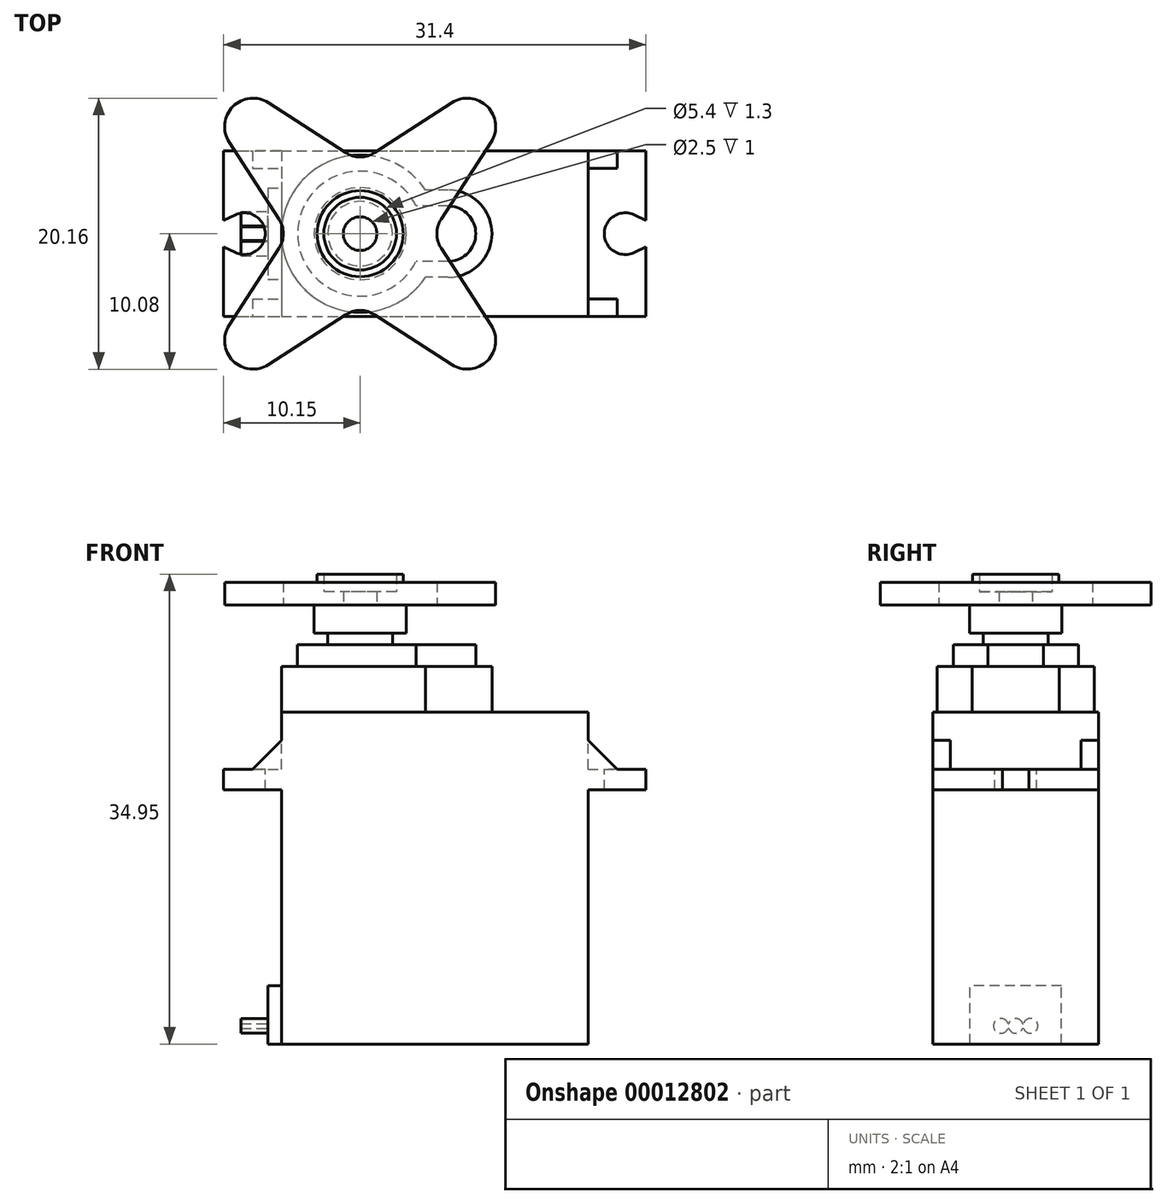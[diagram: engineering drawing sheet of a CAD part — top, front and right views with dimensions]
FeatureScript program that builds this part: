
annotation { "Feature Type Name" : "Feature", "Feature Type Description" : "" }
export const myFeature = defineFeature(function(context is Context, id is Id, definition is map)
    precondition{}
    {
        {
            var Q0;
            Q0=qCreatedBy(makeId("Top.planeOp"),FACE);
            var sketch = newSketch(context, id + "F0", { "sketchPlane" : qUnion([Q0])});
            skArc(sketch, "E0", {"start": v(4.86, 3.25) * mm, "mid": v(-5.85, 0) * mm, "end": v(4.86, -3.25) * mm});
            skLineSegment(sketch, "E1.bottom", {"start": v(-10.15, 6.15) * mm, "end": v(21.25, 6.15) * mm});
            skLineSegment(sketch, "E1.top", {"start": v(-10.15, -6.15) * mm, "end": v(21.25, -6.15) * mm});
            skLineSegment(sketch, "E1.left", {"start": v(-10.15, 6.15) * mm, "end": v(-10.15, 0) * mm});
            skLineSegment(sketch, "E1.right", {"start": v(21.25, 6.15) * mm, "end": v(21.25, 0) * mm});
            skLineSegment(sketch, "E2", {"start": v(-5.85, 6.15) * mm, "end": v(-5.85, -6.15) * mm});
            skLineSegment(sketch, "E3", {"start": v(16.95, 6.15) * mm, "end": v(16.95, -6.15) * mm});
            skCircle(sketch, "E4", {"center": v(-8.6, 0) * mm, "radius": 1.55 * mm});
            skPoint(sketch, "E5", {"position": v(21.25, 0) * mm});
            skLineSegment(sketch, "E6", {"start": v(5.55, 6.15) * mm, "end": v(5.55, -6.15) * mm, "construction": true});
            skArc(sketch, "E7", {"start": v(6.55, -3.25) * mm, "mid": v(9.8, 0) * mm, "end": v(6.55, 3.25) * mm});
            skLineSegment(sketch, "E8", {"start": v(6.55, -3.25) * mm, "end": v(4.86, -3.25) * mm});
            skLineSegment(sketch, "E9", {"start": v(6.55, 3.25) * mm, "end": v(4.86, 3.25) * mm});
            skArc(sketch, "E10.0", {"start": v(4.17, 2.05) * mm, "mid": v(-4.65, 0) * mm, "end": v(4.17, -2.05) * mm});
            skLineSegment(sketch, "E10.1", {"start": v(6.55, 2.05) * mm, "end": v(4.17, 2.05) * mm});
            skArc(sketch, "E10.2", {"start": v(6.55, -2.05) * mm, "mid": v(8.6, 0) * mm, "end": v(6.55, 2.05) * mm});
            skLineSegment(sketch, "E10.3", {"start": v(6.55, -2.05) * mm, "end": v(4.17, -2.05) * mm});
            skCircle(sketch, "E11", {"center": v(0, 0) * mm, "radius": 2.4 * mm});
            skLineSegment(sketch, "E12", {"start": v(-10.15, 0) * mm, "end": v(-10.15, -6.15) * mm});
            skLineSegment(sketch, "E13", {"start": v(21.25, 0) * mm, "end": v(21.25, -6.15) * mm});
            skLineSegment(sketch, "E14", {"start": v(-9.28, 1.4) * mm, "end": v(-12.15, 0) * mm});
            skLineSegment(sketch, "E15", {"start": v(-12.15, 0) * mm, "end": v(-9.28, -1.4) * mm});
            skCircle(sketch, "E16.0.MirrorC", {"center": v(19.7, 0) * mm, "radius": 1.55 * mm});
            skLineSegment(sketch, "E17.0.MirrorCS", {"start": v(20.38, 1.4) * mm, "end": v(23.25, 0) * mm});
            skLineSegment(sketch, "E18.0.MirrorCS", {"start": v(23.25, 0) * mm, "end": v(20.38, -1.4) * mm});
            skSolve(sketch);
        }
        {
            var Q0;
            {var subQ1=sQuery(id+"F0.wireOp",EDGE,"E3");Q0=makeQuery(id+"F0.imprint","IMPRINT",FACE,{"disambiguationData":[TD([[makeQuery(id+"F0.imprint","IMPRINT",EDGE,{"derivedFrom":subQ1}),-1.0]])]});}
            var Q1;
            Q1=makeQuery(id+"F0.imprint","IMPRINT",FACE,{"disambiguationData":[TD([[makeQuery(id+"F0.imprint","IMPRINT",EDGE,{"derivedFrom":sQuery(id+"F0.wireOp",EDGE,"E7")}),1.0]])]});
            var Q2;
            Q2=makeQuery(id+"F0.imprint","IMPRINT",FACE,{"disambiguationData":[TD([[makeQuery(id+"F0.imprint","IMPRINT",EDGE,{"derivedFrom":sQuery(id+"F0.wireOp",EDGE,"E10.0")}),1.0]])]});
            var Q3;
            Q3=makeQuery(id+"F0.imprint","IMPRINT",FACE,{"disambiguationData":[TD([[makeQuery(id+"F0.imprint","IMPRINT",EDGE,{"derivedFrom":sQuery(id+"F0.wireOp",EDGE,"E11")}),1.0]])]});
            extrude(context, id + "F1", {"entities" : qUnion([Q0, Q1, Q2, Q3]), "oppositeDirection" : true, "depth" : 24.7 * mm});
        }
        {
            var Q0;
            Q0=makeQuery(id+"F0.imprint","IMPRINT",FACE,{"disambiguationData":[TD([[makeQuery(id+"F0.imprint","IMPRINT",EDGE,{"derivedFrom":sQuery(id+"F0.wireOp",EDGE,"E7")}),1.0]])]});
            extrude(context, id + "F2", {"entities" : qUnion([Q0]), "operationType" : NewBodyOperationType.ADD, "depth" : (28.1 - 24.7) * mm});
        }
        {
            var Q0;
            Q0=makeQuery(id+"F0.imprint","IMPRINT",FACE,{"disambiguationData":[TD([[makeQuery(id+"F0.imprint","IMPRINT",EDGE,{"derivedFrom":sQuery(id+"F0.wireOp",EDGE,"E10.0")}),1.0]])]});
            extrude(context, id + "F3", {"entities" : qUnion([Q0]), "operationType" : NewBodyOperationType.ADD, "depth" : (29.7 - 24.7) * mm});
        }
        {
            var Q0;
            Q0=makeQuery(id+"F0.imprint","IMPRINT",FACE,{"disambiguationData":[TD([[makeQuery(id+"F0.imprint","IMPRINT",EDGE,{"derivedFrom":sQuery(id+"F0.wireOp",EDGE,"E11")}),1.0]])]});
            extrude(context, id + "F4", {"entities" : qUnion([Q0]), "operationType" : NewBodyOperationType.ADD, "depth" : (32.65 - 24.7) * mm});
        }
        {
            var Q0;
            {var subQ6=sQuery(id+"F0.wireOp",EDGE,"E1.left");var subQ14=sQuery(id+"F0.wireOp",EDGE,"E1.bottom");var subQ16=makeQuery(id+"F0.imprint","INTERSECT",VERTEX,{"derivedFrom":[subQ14,subQ6]});Q0=makeQuery(id+"F0.imprint","IMPRINT",FACE,{"disambiguationData":[TD([[makeQuery(id+"F0.imprint","IMPRINT",EDGE,{"disambiguationData":[TD([[subQ16,-1.0]])],"derivedFrom":subQ14}),-1.0]])]});}
            var Q1;
            {var subQ11=sQuery(id+"F0.wireOp",EDGE,"E3");Q1=makeQuery(id+"F0.imprint","IMPRINT",FACE,{"disambiguationData":[TD([[makeQuery(id+"F0.imprint","IMPRINT",EDGE,{"derivedFrom":subQ11}),1.0]])]});}
            extrude(context, id + "F5", {"entities" : qUnion([Q0, Q1]), "operationType" : NewBodyOperationType.ADD, "oppositeDirection" : true, "depth" : 5.8 * mm, "hasSecondDirection" : true, "secondDirectionOppositeDirection" : true, "secondDirectionDepth" : (5.8 - 1.55) * mm});
        }
        {
            var Q0;
            {var subQ0=sQuery(id+"F0.wireOp",EDGE,"E2");var subQ1=sQuery(id+"F0.wireOp",EDGE,"E1.top");var subQ3=sQuery(id+"F0.wireOp",EDGE,"E1.bottom");var subQ4=sQuery(id+"F0.wireOp",EDGE,"E3");Q0=makeQuery(id+"F5.boolean.opBoolean","SPLIT",FACE,{"disambiguationData":[TD([makeQuery(id+"F1.opExtrude","CAP_FACE",FACE,{"disambiguationData":[OSD([subQ3,subQ1,subQ0,subQ4])],"isStart":false})])],"derivedFrom":makeQuery(id+"F1.opExtrude","SWEPT_FACE",FACE,{"disambiguationData":[OSD([subQ0])]})});}
            var sketch = newSketch(context, id + "F6", { "sketchPlane" : qUnion([Q0])});
            skLineSegment(sketch, "E19.bottom", {"start": v(-3.4, -24.7) * mm, "end": v(3.4, -24.7) * mm});
            skLineSegment(sketch, "E19.top", {"start": v(-3.4, -20.35) * mm, "end": v(3.4, -20.35) * mm});
            skLineSegment(sketch, "E19.left", {"start": v(-3.4, -24.7) * mm, "end": v(-3.4, -20.35) * mm});
            skLineSegment(sketch, "E19.right", {"start": v(3.4, -24.7) * mm, "end": v(3.4, -20.35) * mm});
            skCircle(sketch, "E20", {"center": v(0, -23.35) * mm, "radius": 0.55 * mm});
            skCircle(sketch, "E21", {"center": v(1.1, -23.35) * mm, "radius": 0.55 * mm});
            skCircle(sketch, "E22", {"center": v(-1.1, -23.35) * mm, "radius": 0.55 * mm});
            skLineSegment(sketch, "E23", {"start": v(0, 0) * mm, "end": v(0, -24.7) * mm, "construction": true});
            skLineSegment(sketch, "E24.rect.bottom", {"start": v(1.1, -23.17) * mm, "end": v(-1.1, -23.17) * mm});
            skLineSegment(sketch, "E24.rect.top", {"start": v(1.1, -23.53) * mm, "end": v(-1.1, -23.53) * mm});
            skLineSegment(sketch, "E24.rect.left", {"start": v(1.1, -23.17) * mm, "end": v(1.1, -23.53) * mm});
            skLineSegment(sketch, "E24.rect.right", {"start": v(-1.1, -23.17) * mm, "end": v(-1.1, -23.53) * mm});
            skSolve(sketch);
        }
        {
            var Q0;
            Q0=makeQuery(id+"F6.imprint","IMPRINT",FACE,{"disambiguationData":[TD([[makeQuery(id+"F6.imprint","IMPRINT",EDGE,{"derivedFrom":sQuery(id+"F6.wireOp",EDGE,"E19.bottom")}),1.0]])]});
            extrude(context, id + "F7", {"entities" : qUnion([Q0]), "operationType" : NewBodyOperationType.ADD, "depth" : 1 * mm});
        }
        {
            var Q0;
            {var subQ0=sQuery(id+"F0.wireOp",EDGE,"E2");var subQ1=sQuery(id+"F0.wireOp",EDGE,"E1.top");var subQ3=sQuery(id+"F0.wireOp",EDGE,"E1.bottom");var subQ4=sQuery(id+"F0.wireOp",EDGE,"E3");var subQ10=sQuery(id+"F6.wireOp",EDGE,"E21");Q0=makeQuery(id+"F7.boolean.opBoolean","SPLIT",FACE,{"disambiguationData":[TD([makeQuery(id+"F7.opExtrude","SWEPT_FACE",FACE,{"disambiguationData":[OSD([subQ10])]})])],"derivedFrom":makeQuery(id+"F5.boolean.opBoolean","SPLIT",FACE,{"disambiguationData":[TD([makeQuery(id+"F1.opExtrude","CAP_FACE",FACE,{"disambiguationData":[OSD([subQ3,subQ1,subQ0,subQ4])],"isStart":false})])],"derivedFrom":makeQuery(id+"F1.opExtrude","SWEPT_FACE",FACE,{"disambiguationData":[OSD([subQ0])]})})});}
            extrude(context, id + "F8", {"entities" : qUnion([Q0]), "operationType" : NewBodyOperationType.ADD, "depth" : 3 * mm});
        }
        {
            var Q0;
            Q0=makeQuery(id+"F4.opExtrude","CAP_FACE",FACE,{"disambiguationData":[OSD([sQuery(id+"F0.wireOp",EDGE,"E11")])],"isStart":false});
            var sketch = newSketch(context, id + "F9", { "sketchPlane" : qUnion([Q0])});
            skCircle(sketch, "E25.0", {"center": v(0, 0) * mm, "radius": 2.4 * mm});
            skCircle(sketch, "E26", {"center": v(0, 0) * mm, "radius": 3.43 * mm});
            skLineSegment(sketch, "E27.rect.bottom", {"start": v(10.07, 10.07) * mm, "end": v(-10.07, 10.08) * mm, "construction": true});
            skLineSegment(sketch, "E27.rect.top", {"start": v(10.07, -10.07) * mm, "end": v(-10.08, -10.07) * mm, "construction": true});
            skLineSegment(sketch, "E27.rect.left", {"start": v(10.07, 10.07) * mm, "end": v(10.07, -10.08) * mm, "construction": true});
            skLineSegment(sketch, "E27.rect.right", {"start": v(-10.07, 10.07) * mm, "end": v(-10.07, -10.07) * mm, "construction": true});
            skLineSegment(sketch, "E28", {"start": v(-10.07, 10.08) * mm, "end": v(10.07, -10.07) * mm, "construction": true});
            skArc(sketch, "E29", {"start": v(-6.82, 9.74) * mm, "mid": v(-9.46, 9.46) * mm, "end": v(-9.74, 6.82) * mm});
            skCircle(sketch, "E30", {"center": v(0, 0) * mm, "radius": 4.47 * mm, "construction": true});
            skLineSegment(sketch, "E31", {"start": v(-6.82, 9.74) * mm, "end": v(2.43, 3.76) * mm});
            skLineSegment(sketch, "E32.0.MirrorCS", {"start": v(-9.74, 6.82) * mm, "end": v(-3.76, -2.43) * mm});
            skLineSegment(sketch, "E33.1.0", {"start": v(-9.74, -6.82) * mm, "end": v(-3.76, 2.43) * mm});
            skArc(sketch, "E33.1.1", {"start": v(-9.74, -6.82) * mm, "mid": v(-9.46, -9.46) * mm, "end": v(-6.82, -9.74) * mm});
            skLineSegment(sketch, "E33.1.2", {"start": v(-6.82, -9.74) * mm, "end": v(2.43, -3.76) * mm});
            skLineSegment(sketch, "E33.2.0", {"start": v(6.82, -9.74) * mm, "end": v(-2.43, -3.76) * mm});
            skArc(sketch, "E33.2.1", {"start": v(6.82, -9.74) * mm, "mid": v(9.46, -9.46) * mm, "end": v(9.74, -6.82) * mm});
            skLineSegment(sketch, "E33.2.2", {"start": v(9.74, -6.82) * mm, "end": v(3.76, 2.43) * mm});
            skLineSegment(sketch, "E33.3.0", {"start": v(9.74, 6.82) * mm, "end": v(3.76, -2.43) * mm});
            skArc(sketch, "E33.3.1", {"start": v(9.74, 6.82) * mm, "mid": v(9.46, 9.46) * mm, "end": v(6.82, 9.74) * mm});
            skLineSegment(sketch, "E33.3.2", {"start": v(6.82, 9.74) * mm, "end": v(-2.43, 3.76) * mm});
            skCircle(sketch, "E34", {"center": v(0, 0) * mm, "radius": 3.2 * mm});
            skCircle(sketch, "E35", {"center": v(0, 0) * mm, "radius": 2.7 * mm});
            skCircle(sketch, "E36", {"center": v(0, 0) * mm, "radius": 1.25 * mm});
            skSolve(sketch);
        }
        {
            var Q0;
            Q0=makeQuery(id+"F9.imprint","IMPRINT",FACE,{"disambiguationData":[TD([[makeQuery(id+"F9.imprint","IMPRINT",EDGE,{"derivedFrom":sQuery(id+"F9.wireOp",EDGE,"E26")}),1.0]])]});
            var Q1;
            Q1=makeQuery(id+"F9.imprint","IMPRINT",FACE,{"disambiguationData":[TD([[makeQuery(id+"F9.imprint","IMPRINT",EDGE,{"derivedFrom":sQuery(id+"F9.wireOp",EDGE,"E34")}),1.0]])]});
            var Q2;
            Q2=makeQuery(id+"F9.imprint","IMPRINT",FACE,{"disambiguationData":[TD([[makeQuery(id+"F9.imprint","IMPRINT",EDGE,{"derivedFrom":sQuery(id+"F9.wireOp",EDGE,"E25.0")}),-1.0]])]});
            extrude(context, id + "F10", {"entities" : qUnion([Q0, Q1, Q2]), "oppositeDirection" : true, "depth" : 2.1 * mm});
        }
        {
            var Q0;
            Q0=makeQuery(id+"F9.imprint","IMPRINT",FACE,{"disambiguationData":[TD([[makeQuery(id+"F9.imprint","IMPRINT",EDGE,{"derivedFrom":sQuery(id+"F9.wireOp",EDGE,"E26")}),-1.0]])]});
            var Q1;
            Q1=makeQuery(id+"F9.imprint","IMPRINT",FACE,{"disambiguationData":[TD([[makeQuery(id+"F9.imprint","IMPRINT",EDGE,{"derivedFrom":sQuery(id+"F9.wireOp",EDGE,"E26")}),1.0]])]});
            var Q2;
            Q2=makeQuery(id+"F9.imprint","IMPRINT",FACE,{"disambiguationData":[TD([[makeQuery(id+"F9.imprint","IMPRINT",EDGE,{"derivedFrom":sQuery(id+"F9.wireOp",EDGE,"E34")}),1.0]])]});
            extrude(context, id + "F11", {"entities" : qUnion([Q0, Q1, Q2]), "operationType" : NewBodyOperationType.ADD, "depth" : 1.7 * mm});
        }
        {
            var Q0;
            Q0=makeQuery(id+"F9.imprint","IMPRINT",FACE,{"disambiguationData":[TD([[makeQuery(id+"F9.imprint","IMPRINT",EDGE,{"derivedFrom":sQuery(id+"F9.wireOp",EDGE,"E34")}),1.0]])]});
            extrude(context, id + "F12", {"entities" : qUnion([Q0]), "operationType" : NewBodyOperationType.ADD, "depth" : 2.3 * mm});
        }
        {
            var Q0;
            Q0=makeQuery(id+"F9.imprint","IMPRINT",FACE,{"disambiguationData":[TD([[makeQuery(id+"F9.imprint","IMPRINT",EDGE,{"derivedFrom":sQuery(id+"F9.wireOp",EDGE,"E25.0")}),1.0]])]});
            var Q1;
            Q1=makeQuery(id+"F9.imprint","IMPRINT",FACE,{"disambiguationData":[TD([[makeQuery(id+"F9.imprint","IMPRINT",EDGE,{"derivedFrom":sQuery(id+"F9.wireOp",EDGE,"E25.0")}),-1.0]])]});
            extrude(context, id + "F13", {"entities" : qUnion([Q0, Q1]), "operationType" : NewBodyOperationType.ADD, "depth" : 1 * mm});
        }
        {
            var Q0;
            Q0=makeQuery(id+"F11.opExtrude","SWEPT_EDGE",EDGE,{"disambiguationData":[OSD([sQuery(id+"F9.wireOp",EDGE,"E31"),sQuery(id+"F9.wireOp",EDGE,"E33.3.2")])]});
            var Q1;
            Q1=makeQuery(id+"F11.opExtrude","SWEPT_EDGE",EDGE,{"disambiguationData":[OSD([sQuery(id+"F9.wireOp",EDGE,"E33.2.2"),sQuery(id+"F9.wireOp",EDGE,"E33.3.0")])]});
            var Q2;
            Q2=makeQuery(id+"F11.opExtrude","SWEPT_EDGE",EDGE,{"disambiguationData":[OSD([sQuery(id+"F9.wireOp",EDGE,"E33.1.2"),sQuery(id+"F9.wireOp",EDGE,"E33.2.0")])]});
            var Q3;
            Q3=makeQuery(id+"F11.opExtrude","SWEPT_EDGE",EDGE,{"disambiguationData":[OSD([sQuery(id+"F9.wireOp",EDGE,"E32.0.MirrorCS"),sQuery(id+"F9.wireOp",EDGE,"E33.1.0")])]});
            fillet(context, id + "F14", {"entities" : qUnion([Q0, Q1, Q2, Q3]), "radius" : 2 * mm, "tangentPropagation" : true, "allowEdgeOverflow" : false});
        }
        {
            var Q0;
            {var subQ0=sQuery(id+"F0.wireOp",EDGE,"E1.top");Q0=makeQuery(id+"F5.boolean.opBoolean","MERGE",FACE,{"derivedFrom":[makeQuery(id+"F1.opExtrude","SWEPT_FACE",FACE,{"disambiguationData":[OSD([subQ0])]}),makeQuery(id+"F5.opExtrude","SWEPT_FACE",FACE,{"disambiguationData":[OSD([subQ0]),TDD([makeQuery(id+"F0.imprint","IMPRINT",EDGE,{"disambiguationData":[TD([[makeQuery(id+"F0.imprint","INTERSECT",VERTEX,{"derivedFrom":[subQ0,sQuery(id+"F0.wireOp",EDGE,"E12")]}),-1.0]])],"derivedFrom":subQ0})])]}),makeQuery(id+"F5.opExtrude","SWEPT_FACE",FACE,{"disambiguationData":[OSD([subQ0]),TDD([makeQuery(id+"F0.imprint","IMPRINT",EDGE,{"disambiguationData":[TD([[makeQuery(id+"F0.imprint","INTERSECT",VERTEX,{"derivedFrom":[subQ0,sQuery(id+"F0.wireOp",EDGE,"E13")]}),1.0]])],"derivedFrom":subQ0})])]})]});}
            var sketch = newSketch(context, id + "F15", { "sketchPlane" : qUnion([Q0])});
            skLineSegment(sketch, "E37", {"start": v(19.1, -4.25) * mm, "end": v(16.95, -2.1) * mm});
            skLineSegment(sketch, "E38", {"start": v(16.95, -2.1) * mm, "end": v(16.95, -4.25) * mm});
            skLineSegment(sketch, "E39", {"start": v(16.95, -4.25) * mm, "end": v(19.1, -4.25) * mm});
            skLineSegment(sketch, "E40", {"start": v(5.55, 0) * mm, "end": v(5.55, -4.25) * mm, "construction": true});
            skLineSegment(sketch, "E41.0.MirrorCS", {"start": v(-8, -4.25) * mm, "end": v(-5.85, -2.1) * mm});
            skLineSegment(sketch, "E41.1.MirrorCS", {"start": v(-5.85, -2.1) * mm, "end": v(-5.85, -4.25) * mm});
            skLineSegment(sketch, "E41.2.MirrorCS", {"start": v(-5.85, -4.25) * mm, "end": v(-8, -4.25) * mm});
            skSolve(sketch);
        }
        {
            var Q0;
            Q0 = qSketchRegion(id + "F15", true);
            extrude(context, id + "F16", {"entities" : qUnion([Q0]), "operationType" : NewBodyOperationType.ADD, "oppositeDirection" : true, "depth" : 1.3 * mm});
        }
        {
            var Q0;
            Q0 = qSketchRegion(id + "F15", true);
            var Q1;
            {var subQ0=sQuery(id+"F0.wireOp",EDGE,"E1.bottom");Q1=makeQuery(id+"F5.boolean.opBoolean","MERGE",FACE,{"derivedFrom":[makeQuery(id+"F1.opExtrude","SWEPT_FACE",FACE,{"disambiguationData":[OSD([subQ0])]}),makeQuery(id+"F5.opExtrude","SWEPT_FACE",FACE,{"disambiguationData":[OSD([subQ0]),TDD([makeQuery(id+"F0.imprint","IMPRINT",EDGE,{"disambiguationData":[TD([[makeQuery(id+"F0.imprint","INTERSECT",VERTEX,{"derivedFrom":[subQ0,sQuery(id+"F0.wireOp",EDGE,"E1.left")]}),-1.0]])],"derivedFrom":subQ0})])]}),makeQuery(id+"F5.opExtrude","SWEPT_FACE",FACE,{"disambiguationData":[OSD([subQ0]),TDD([makeQuery(id+"F0.imprint","IMPRINT",EDGE,{"disambiguationData":[TD([[makeQuery(id+"F0.imprint","INTERSECT",VERTEX,{"derivedFrom":[subQ0,sQuery(id+"F0.wireOp",EDGE,"E1.right")]}),1.0]])],"derivedFrom":subQ0})])]})]});}
            extrude(context, id + "F17", {"entities" : qUnion([Q0]), "operationType" : NewBodyOperationType.ADD, "endBound" : BoundingType.UP_TO_SURFACE, "oppositeDirection" : true, "endBoundEntityFace" : qUnion([Q1]), "depth" : 15.5 * mm, "hasSecondDirection" : true, "secondDirectionOppositeDirection" : true, "secondDirectionDepth" : 11 * mm});
        }
    });
